# Revit family: Mixer-Bath Shower-Caroma Saracom with Diverter
name_source: partatom
category: Plumbing Fixtures
revit_build: Autodesk Revit 2014 (Build: 20131024_2115(x64)
units: mm (PartAtom-declared; Revit-internal decimal feet)

## types (1)
- Standard
    Assembly Code = C1030210
    CW Connection = Yes
    CWFU = 3
    Connector Radius = 10 mm  [stored 0.0328084 ft]
    Cost = 0 $
    Default Elevation = 1000 mm  [stored 3.28084 ft]
    Description = The Saracom range offers the home owner the practical choice in using one stylish mixer design for the entire home, from the kitchen to the laundry to the bathroom.
    HW Connection = Yes
    HWFU = 3
    Height_ANZRS = 170 mm  [stored 0.557743 ft]
    Length_ANZRS = 100 mm  [stored 0.328084 ft]
    Manufacturer = GWA Bathrooms & Kitchens
    Material_ANZRS = Metal-Chrome-Caroma
    Model = 98024C
    ModifiedIssue_ANZRS = 20150109.01 $
    Type Comments = Caroma Saracom Bath/Shower Mixer with Diverter
    URL = http://specify.caroma.com.au
    Vent Connection = No
    Waste Connection = No
    Width_ANZRS = 109 mm  [stored 0.357612 ft]

note: [stored X ft] marks values corroborated as IEEE doubles in the binary element streams (Revit-internal decimal feet)

## geometry (parser evidence)
native form markers: Blend x10, Sweep x1
no freeform markers — native parametric forms only
